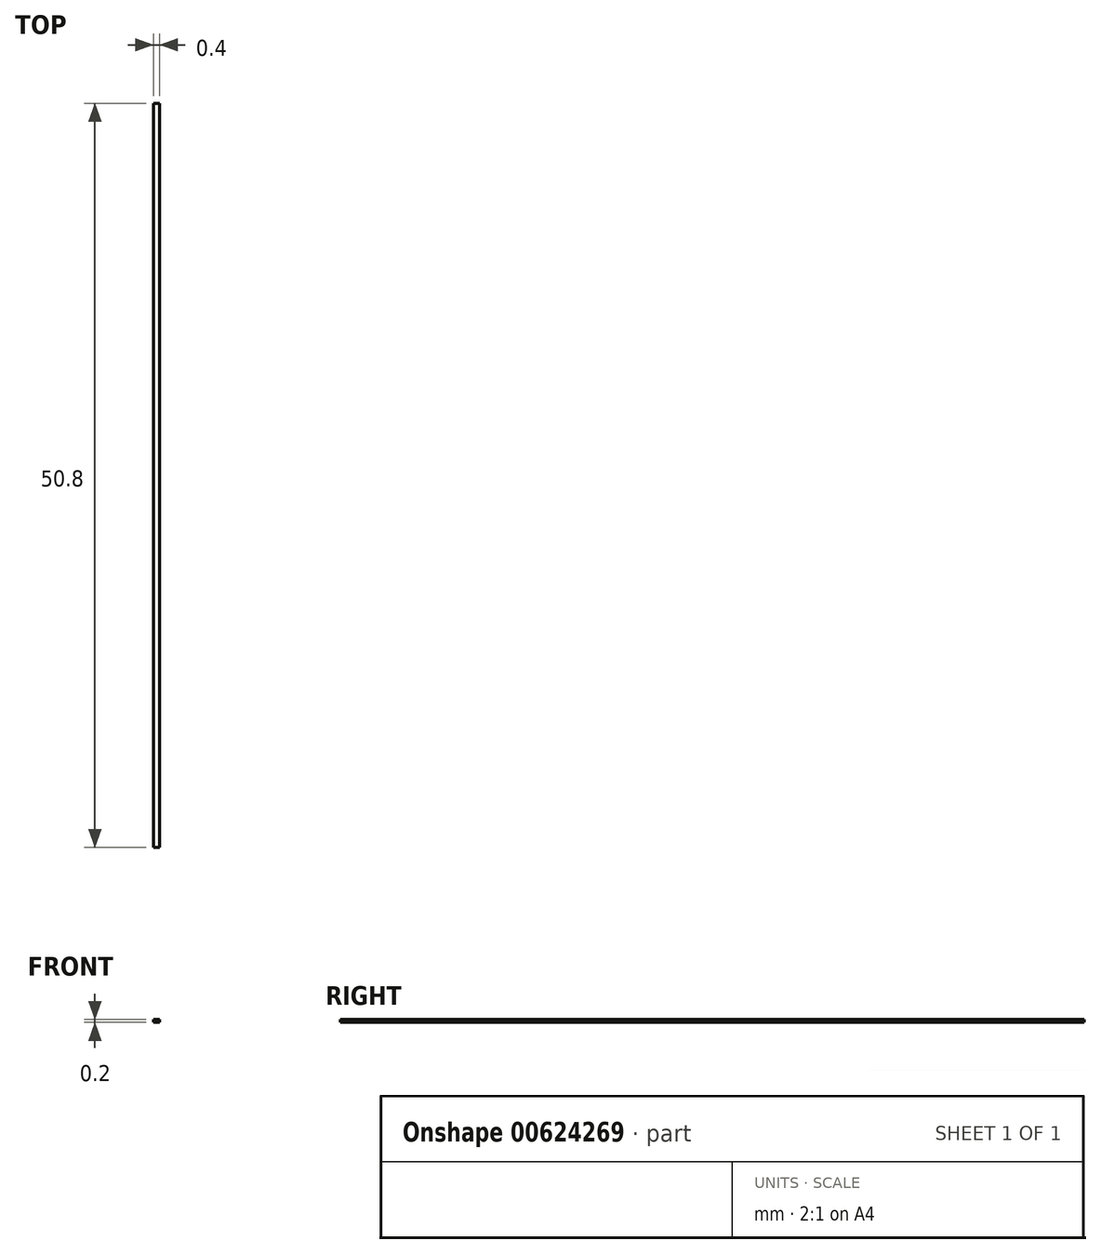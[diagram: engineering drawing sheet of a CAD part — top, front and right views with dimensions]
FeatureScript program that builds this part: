
annotation { "Feature Type Name" : "Feature", "Feature Type Description" : "" }
export const myFeature = defineFeature(function(context is Context, id is Id, definition is map)
    precondition{}
    {
        {
            var Q0;
            Q0=qCreatedBy(makeId("Top.planeOp"),FACE);
            var sketch = newSketch(context, id + "F0", { "sketchPlane" : qUnion([Q0])});
            skLineSegment(sketch, "E0.bottom", {"start": v(-8.95, 45.94) * mm, "end": v(-8.55, 45.94) * mm});
            skLineSegment(sketch, "E0.top", {"start": v(-8.95, -4.86) * mm, "end": v(-8.55, -4.86) * mm});
            skLineSegment(sketch, "E0.left", {"start": v(-8.95, 45.94) * mm, "end": v(-8.95, -4.86) * mm});
            skLineSegment(sketch, "E0.right", {"start": v(-8.55, 45.94) * mm, "end": v(-8.55, -4.86) * mm});
            skSolve(sketch);
        }
        {
            var Q0;
            Q0 = qSketchRegion(id + "F0", true);
            extrude(context, id + "F1", {"entities" : qUnion([Q0]), "depth" : 0.2 * mm, "offsetDistance" : 25.4 * mm});
        }
    });
